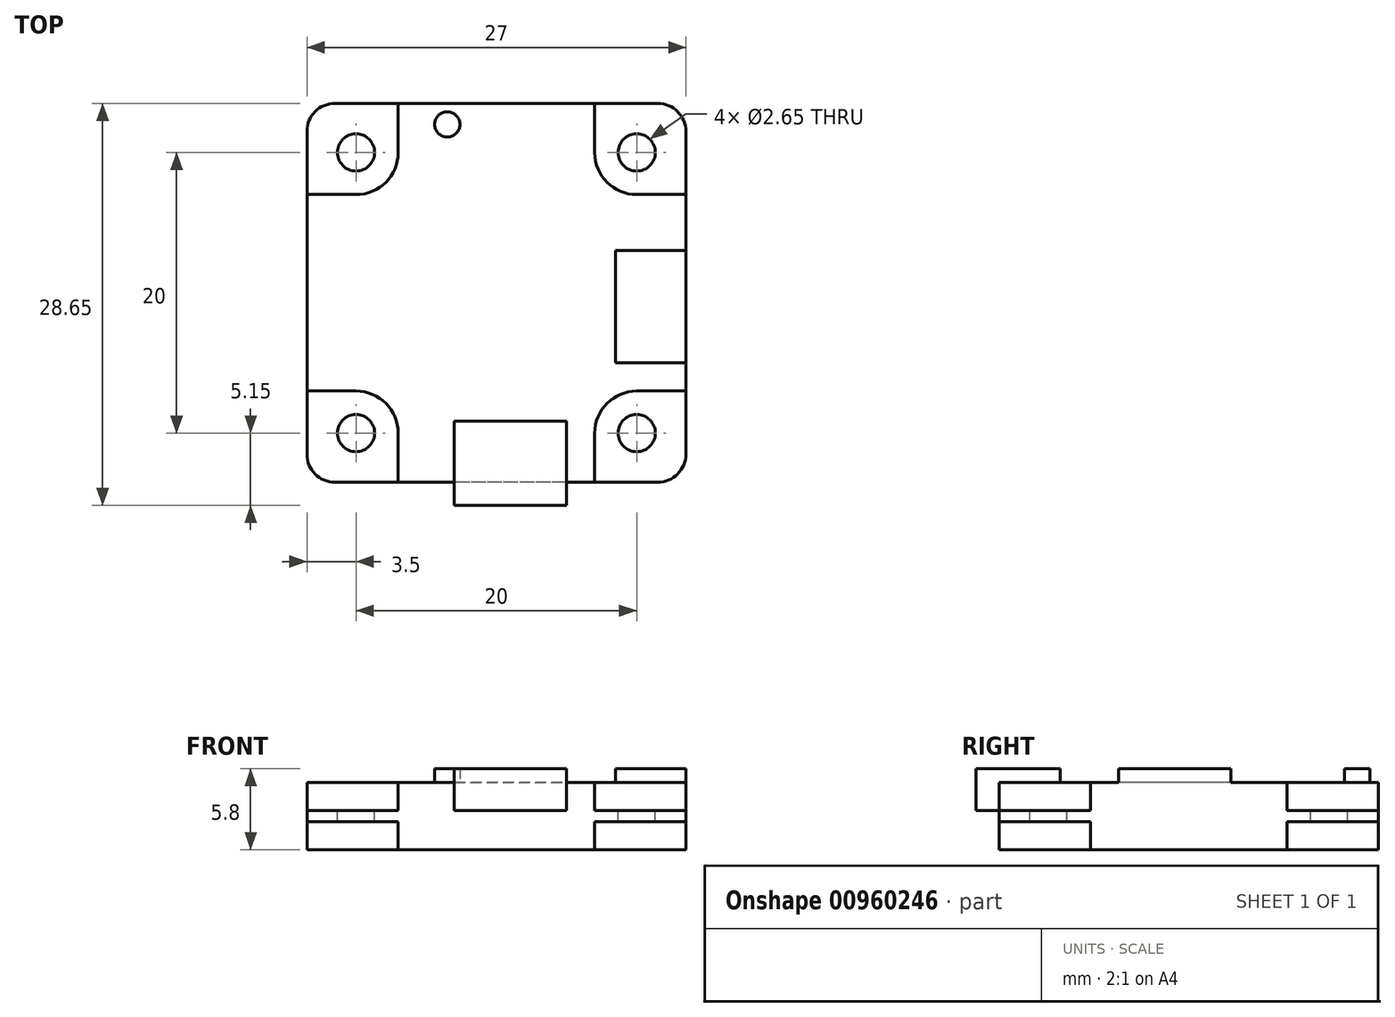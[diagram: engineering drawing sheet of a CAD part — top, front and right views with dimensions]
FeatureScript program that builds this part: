
annotation { "Feature Type Name" : "Feature", "Feature Type Description" : "" }
export const myFeature = defineFeature(function(context is Context, id is Id, definition is map)
    precondition{}
    {
        {
            var Q0;
            Q0=qCreatedBy(makeId("Top.planeOp"),FACE);
            var sketch = newSketch(context, id + "F0", { "sketchPlane" : qUnion([Q0])});
            skLineSegment(sketch, "E0.bottom", {"start": v(13.5, 13.5) * mm, "end": v(-13.5, 13.5) * mm});
            skLineSegment(sketch, "E0.top", {"start": v(13.5, -13.5) * mm, "end": v(-13.5, -13.5) * mm});
            skLineSegment(sketch, "E0.left", {"start": v(13.5, 13.5) * mm, "end": v(13.5, -13.5) * mm});
            skLineSegment(sketch, "E0.right", {"start": v(-13.5, 13.5) * mm, "end": v(-13.5, -13.5) * mm});
            skPoint(sketch, "E0.middle", {"position": v(0, 0) * mm});
            skLineSegment(sketch, "E1.bottom", {"start": v(10, 10) * mm, "end": v(-10, 10) * mm, "construction": true});
            skLineSegment(sketch, "E1.top", {"start": v(10, -10) * mm, "end": v(-10, -10) * mm, "construction": true});
            skLineSegment(sketch, "E1.left", {"start": v(10, 10) * mm, "end": v(10, -10) * mm, "construction": true});
            skLineSegment(sketch, "E1.right", {"start": v(-10, 10) * mm, "end": v(-10, -10) * mm, "construction": true});
            skSolve(sketch);
        }
        {
            var Q0;
            Q0=makeQuery(id+"F0.imprint","IMPRINT",FACE,{"disambiguationData":[TD([[makeQuery(id+"F0.imprint","IMPRINT",EDGE,{"derivedFrom":sQuery(id+"F0.wireOp",EDGE,"E0.bottom")}),1.0]])]});
            extrude(context, id + "F1", {"entities" : qUnion([Q0]), "depth" : 0.8 * mm, "offsetDistance" : 25 * mm});
        }
        {
            var Q0;
            Q0=sQuery(id+"F0.wireOp",VERTEX,"E1.bottom.end");
            var Q1;
            Q1=sQuery(id+"F0.wireOp",VERTEX,"E1.top.end");
            var Q2;
            Q2=sQuery(id+"F0.wireOp",VERTEX,"E1.bottom.start");
            var Q3;
            Q3=sQuery(id+"F0.wireOp",VERTEX,"E1.top.start");
            var Q4;
            Q4=makeQuery(id+"F1.opExtrude","SWEPT_BODY",BODY,{"disambiguationData":[OSD([sQuery(id+"F0.wireOp",EDGE,"E0.bottom"),sQuery(id+"F0.wireOp",EDGE,"E0.top"),sQuery(id+"F0.wireOp",EDGE,"E0.left"),sQuery(id+"F0.wireOp",EDGE,"E0.right")])]});
            hole(context, id + "F2", {"style" : HoleStyle.SIMPLE, "endStyle" : HoleEndStyle.THROUGH, "oppositeDirection" : true, "holeDiameter" : 2.65 * mm, "majorDiameter" : 5 * mm, "isTappedThrough" : true, "tappedDepth" : 12 * mm, "tapClearance" : 3, "locations" : qUnion([Q0, Q1, Q2, Q3]), "scope" : qUnion([Q4])});
        }
        {
            var Q0;
            Q0=makeQuery(id+"F1.opExtrude","SWEPT_EDGE",EDGE,{"disambiguationData":[OSD([sQuery(id+"F0.wireOp",EDGE,"E0.top"),sQuery(id+"F0.wireOp",EDGE,"E0.right")])]});
            var Q1;
            Q1=makeQuery(id+"F1.opExtrude","SWEPT_EDGE",EDGE,{"disambiguationData":[OSD([sQuery(id+"F0.wireOp",EDGE,"E0.bottom"),sQuery(id+"F0.wireOp",EDGE,"E0.right")])]});
            var Q2;
            Q2=makeQuery(id+"F1.opExtrude","SWEPT_EDGE",EDGE,{"disambiguationData":[OSD([sQuery(id+"F0.wireOp",EDGE,"E0.top"),sQuery(id+"F0.wireOp",EDGE,"E0.left")])]});
            var Q3;
            Q3=makeQuery(id+"F1.opExtrude","SWEPT_EDGE",EDGE,{"disambiguationData":[OSD([sQuery(id+"F0.wireOp",EDGE,"E0.bottom"),sQuery(id+"F0.wireOp",EDGE,"E0.left")])]});
            fillet(context, id + "F3", {"entities" : qUnion([Q0, Q1, Q2, Q3]), "radius" : 2 * mm, "tangentPropagation" : true, "allowEdgeOverflow" : false});
        }
        {
            var Q0;
            Q0=makeQuery(id+"F1.opExtrude","CAP_FACE",FACE,{"disambiguationData":[OSD([sQuery(id+"F0.wireOp",EDGE,"E0.bottom"),sQuery(id+"F0.wireOp",EDGE,"E0.top"),sQuery(id+"F0.wireOp",EDGE,"E0.left"),sQuery(id+"F0.wireOp",EDGE,"E0.right")])],"isStart":false});
            var sketch = newSketch(context, id + "F4", { "sketchPlane" : qUnion([Q0])});
            skLineSegment(sketch, "E2.bottom", {"start": v(8.5, 3) * mm, "end": v(13.5, 3) * mm});
            skLineSegment(sketch, "E2.top", {"start": v(8.5, -5) * mm, "end": v(13.5, -5) * mm});
            skLineSegment(sketch, "E2.left", {"start": v(8.5, 3) * mm, "end": v(8.5, -5) * mm});
            skLineSegment(sketch, "E2.right", {"start": v(13.5, 3) * mm, "end": v(13.5, -5) * mm});
            skLineSegment(sketch, "E3.bottom", {"start": v(-3, -9.15) * mm, "end": v(5, -9.15) * mm});
            skLineSegment(sketch, "E3.top", {"start": v(-3, -15.15) * mm, "end": v(5, -15.15) * mm});
            skLineSegment(sketch, "E3.left", {"start": v(-3, -9.15) * mm, "end": v(-3, -15.15) * mm});
            skLineSegment(sketch, "E3.right", {"start": v(5, -9.15) * mm, "end": v(5, -15.15) * mm});
            skCircle(sketch, "E4", {"center": v(-3.5, 12) * mm, "radius": 0.9 * mm});
            skSolve(sketch);
        }
        {
            var Q0;
            Q0=qSketchRegion(id+"F4",true);
            extrude(context, id + "F5", {"entities" : qUnion([Q0]), "operationType" : NewBodyOperationType.ADD, "depth" : 3 * mm, "offsetDistance" : 25 * mm});
        }
        {
            var Q0;
            Q0=qCreatedBy(makeId("Top.planeOp"),FACE);
            var sketch = newSketch(context, id + "F6", { "sketchPlane" : qUnion([Q0])});
            skLineSegment(sketch, "E5.0.10", {"start": v(7, 13.5) * mm, "end": v(-7, 13.5) * mm});
            skLineSegment(sketch, "E5.0.12", {"start": v(-13.5, 7) * mm, "end": v(-13.5, -7) * mm});
            skCircle(sketch, "E6.0", {"center": v(-10, 10) * mm, "radius": 1.32 * mm, "construction": true});
            skLineSegment(sketch, "E7", {"start": v(-7, 10) * mm, "end": v(-7, 13.5) * mm});
            skLineSegment(sketch, "E8", {"start": v(-10, 7) * mm, "end": v(-13.5, 7) * mm});
            skArc(sketch, "E9", {"start": v(-7, 10) * mm, "mid": v(-7.88, 7.88) * mm, "end": v(-10, 7) * mm});
            skLineSegment(sketch, "E10.MirrorCS", {"start": v(10, 7) * mm, "end": v(13.5, 7) * mm});
            skArc(sketch, "E11.MirrorCS", {"start": v(7, 10) * mm, "mid": v(7.88, 7.88) * mm, "end": v(10, 7) * mm});
            skLineSegment(sketch, "E12.MirrorCS", {"start": v(7, 10) * mm, "end": v(7, 13.5) * mm});
            skLineSegment(sketch, "E13.MirrorCS", {"start": v(-10, -7) * mm, "end": v(-13.5, -7) * mm});
            skArc(sketch, "E14.MirrorCS", {"start": v(-7, -10) * mm, "mid": v(-7.88, -7.88) * mm, "end": v(-10, -7) * mm});
            skLineSegment(sketch, "E15.MirrorCS", {"start": v(-7, -10) * mm, "end": v(-7, -13.5) * mm});
            skLineSegment(sketch, "E16.MirrorCS", {"start": v(7, -10) * mm, "end": v(7, -13.5) * mm});
            skArc(sketch, "E17.MirrorCS", {"start": v(7, -10) * mm, "mid": v(7.88, -7.88) * mm, "end": v(10, -7) * mm});
            skLineSegment(sketch, "E18.MirrorCS", {"start": v(10, -7) * mm, "end": v(13.5, -7) * mm});
            skLineSegment(sketch, "E19.0", {"start": v(7, -13.5) * mm, "end": v(-7, -13.5) * mm});
            skLineSegment(sketch, "E20.0", {"start": v(13.5, 7) * mm, "end": v(13.5, -7) * mm});
            skSolve(sketch);
        }
        {
            var Q0;
            Q0=qSketchRegion(id+"F6",true);
            extrude(context, id + "F7", {"entities" : qUnion([Q0]), "operationType" : NewBodyOperationType.ADD, "depth" : 2.8 * mm, "offsetDistance" : 25 * mm, "hasSecondDirection" : true, "secondDirectionOppositeDirection" : true, "secondDirectionDepth" : 2 * mm});
        }
    });
